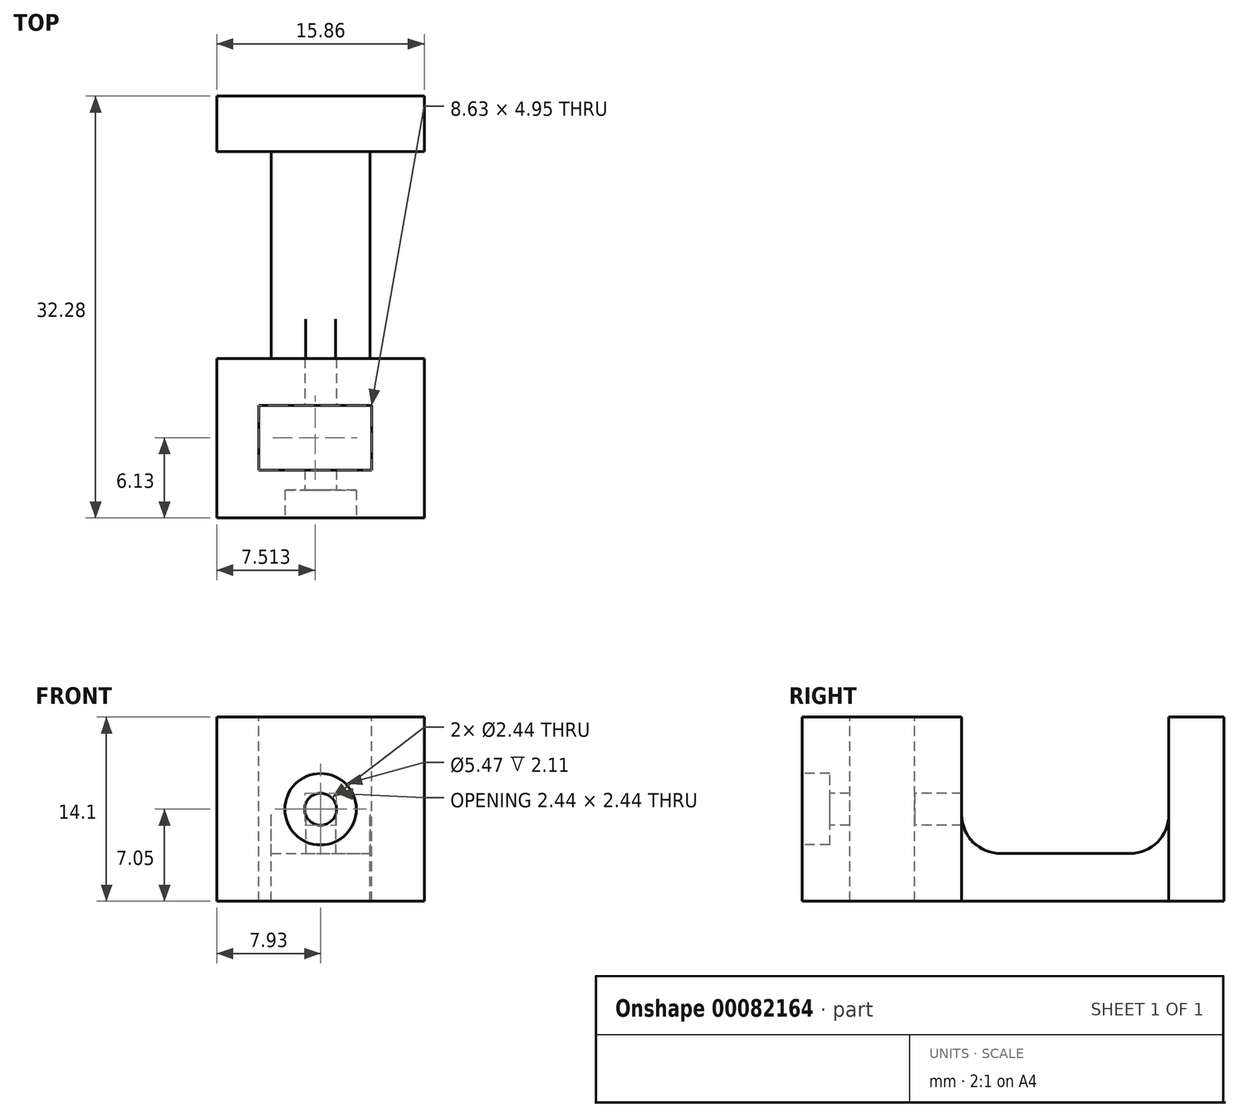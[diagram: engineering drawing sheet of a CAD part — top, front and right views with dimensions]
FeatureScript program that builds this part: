
annotation { "Feature Type Name" : "Feature", "Feature Type Description" : "" }
export const myFeature = defineFeature(function(context is Context, id is Id, definition is map)
    precondition{}
    {
        {
            var Q0;
            Q0=qCreatedBy(makeId("Top.planeOp"),FACE);
            var sketch = newSketch(context, id + "F0", { "sketchPlane" : qUnion([Q0])});
            skLineSegment(sketch, "E0.bottom", {"start": v(7.94, 16.14) * mm, "end": v(-7.93, 16.14) * mm});
            skLineSegment(sketch, "E0.top", {"start": v(7.93, -16.14) * mm, "end": v(-7.94, -16.14) * mm});
            skLineSegment(sketch, "E0.left", {"start": v(7.94, 16.14) * mm, "end": v(7.93, -16.14) * mm});
            skLineSegment(sketch, "E0.right", {"start": v(-7.93, 16.14) * mm, "end": v(-7.94, -16.14) * mm});
            skPoint(sketch, "E0.middle", {"position": v(0, 0) * mm});
            skSolve(sketch);
        }
        {
            var Q0;
            Q0 = qSketchRegion(id + "F0", true);
            extrude(context, id + "F1", {"entities" : qUnion([Q0]), "depth" : 14.1 * mm});
        }
        {
            var Q0;
            Q0=makeQuery(id+"F1.opExtrude","CAP_FACE",FACE,{"disambiguationData":[OSD([sQuery(id+"F0.wireOp",EDGE,"E0.bottom"),sQuery(id+"F0.wireOp",EDGE,"E0.top"),sQuery(id+"F0.wireOp",EDGE,"E0.left"),sQuery(id+"F0.wireOp",EDGE,"E0.right")])],"isStart":false});
            var sketch = newSketch(context, id + "F2", { "sketchPlane" : qUnion([Q0])});
            skLineSegment(sketch, "E1.bottom", {"start": v(-7.93, 11.9) * mm, "end": v(7.94, 11.9) * mm});
            skLineSegment(sketch, "E1.top", {"start": v(-7.93, -3.94) * mm, "end": v(7.94, -3.94) * mm});
            skLineSegment(sketch, "E1.left", {"start": v(-7.93, 11.9) * mm, "end": v(-7.93, -3.94) * mm});
            skLineSegment(sketch, "E1.right", {"start": v(7.94, 11.9) * mm, "end": v(7.94, -3.94) * mm});
            skSolve(sketch);
        }
        {
            var Q0;
            Q0 = qSketchRegion(id + "F2", true);
            extrude(context, id + "F3", {"entities" : qUnion([Q0]), "operationType" : NewBodyOperationType.REMOVE, "oppositeDirection" : true, "depth" : 10.45 * mm});
        }
        {
            var Q0;
            Q0=makeQuery(id+"F3.boolean.opBoolean","COPY",FACE,{"derivedFrom":makeQuery(id+"F3.opExtrude","CAP_FACE",FACE,{"disambiguationData":[OSD([sQuery(id+"F2.wireOp",EDGE,"E1.bottom"),sQuery(id+"F2.wireOp",EDGE,"E1.top"),sQuery(id+"F2.wireOp",EDGE,"E1.left"),sQuery(id+"F2.wireOp",EDGE,"E1.right")])],"isStart":false})});
            var sketch = newSketch(context, id + "F4", { "sketchPlane" : qUnion([Q0])});
            skLineSegment(sketch, "E2.bottom", {"start": v(3.77, 11.9) * mm, "end": v(7.93, 11.9) * mm});
            skLineSegment(sketch, "E2.top", {"start": v(3.77, -3.94) * mm, "end": v(7.93, -3.94) * mm});
            skLineSegment(sketch, "E2.left", {"start": v(3.77, 11.9) * mm, "end": v(3.78, -3.94) * mm});
            skLineSegment(sketch, "E2.right", {"start": v(7.94, 11.9) * mm, "end": v(7.94, -3.94) * mm});
            skLineSegment(sketch, "E3.bottom", {"start": v(-7.93, 11.9) * mm, "end": v(-3.77, 11.9) * mm});
            skLineSegment(sketch, "E3.top", {"start": v(-7.93, -3.94) * mm, "end": v(-3.77, -3.94) * mm});
            skLineSegment(sketch, "E3.left", {"start": v(-7.93, 11.9) * mm, "end": v(-7.93, -3.94) * mm});
            skLineSegment(sketch, "E3.right", {"start": v(-3.77, 11.9) * mm, "end": v(-3.77, -3.94) * mm});
            skSolve(sketch);
        }
        {
            var Q0;
            Q0 = qSketchRegion(id + "F4", true);
            extrude(context, id + "F5", {"entities" : qUnion([Q0]), "operationType" : NewBodyOperationType.REMOVE, "endBound" : BoundingType.UP_TO_NEXT, "oppositeDirection" : true, "depth" : 25 * mm});
        }
        {
            var Q0;
            {var subQ0=sQuery(id+"F0.wireOp",EDGE,"E0.top");var subQ1=sQuery(id+"F0.wireOp",EDGE,"E0.left");var subQ2=sQuery(id+"F0.wireOp",EDGE,"E0.right");Q0=makeQuery(id+"F3.boolean.opBoolean","SPLIT",FACE,{"disambiguationData":[TD([makeQuery(id+"F1.opExtrude","SWEPT_FACE",FACE,{"disambiguationData":[OSD([subQ0])]})])],"derivedFrom":makeQuery(id+"F1.opExtrude","CAP_FACE",FACE,{"disambiguationData":[OSD([sQuery(id+"F0.wireOp",EDGE,"E0.bottom"),subQ0,subQ1,subQ2])],"isStart":false})});}
            var sketch = newSketch(context, id + "F6", { "sketchPlane" : qUnion([Q0])});
            skLineSegment(sketch, "E4.bottom", {"start": v(3.9, -12.49) * mm, "end": v(-4.73, -12.49) * mm});
            skLineSegment(sketch, "E4.top", {"start": v(3.9, -7.54) * mm, "end": v(-4.73, -7.54) * mm});
            skLineSegment(sketch, "E4.left", {"start": v(3.9, -12.49) * mm, "end": v(3.9, -7.54) * mm});
            skLineSegment(sketch, "E4.right", {"start": v(-4.73, -12.49) * mm, "end": v(-4.73, -7.54) * mm});
            skSolve(sketch);
        }
        {
            var Q0;
            Q0 = qSketchRegion(id + "F6", true);
            extrude(context, id + "F7", {"entities" : qUnion([Q0]), "operationType" : NewBodyOperationType.REMOVE, "endBound" : BoundingType.UP_TO_NEXT, "oppositeDirection" : true, "depth" : 25 * mm});
        }
        {
            var Q0;
            Q0=makeQuery(id+"F1.opExtrude","SWEPT_FACE",FACE,{"disambiguationData":[OSD([sQuery(id+"F0.wireOp",EDGE,"E0.top")])]});
            var sketch = newSketch(context, id + "F8", { "sketchPlane" : qUnion([Q0])});
            skCircle(sketch, "E5", {"center": v(0, 7.05) * mm, "radius": 1.22 * mm});
            skSolve(sketch);
        }
        {
            var Q0;
            Q0 = qSketchRegion(id + "F8", true);
            extrude(context, id + "F9", {"entities" : qUnion([Q0]), "operationType" : NewBodyOperationType.REMOVE, "oppositeDirection" : true, "depth" : 12.5 * mm});
        }
        {
            var Q0;
            Q0=makeQuery(id+"F1.opExtrude","SWEPT_FACE",FACE,{"disambiguationData":[OSD([sQuery(id+"F0.wireOp",EDGE,"E0.top")])]});
            var sketch = newSketch(context, id + "F10", { "sketchPlane" : qUnion([Q0])});
            skCircle(sketch, "E6", {"center": v(0, 7.05) * mm, "radius": 2.73 * mm});
            skSolve(sketch);
        }
        {
            var Q0;
            Q0 = qSketchRegion(id + "F10", true);
            extrude(context, id + "F11", {"entities" : qUnion([Q0]), "operationType" : NewBodyOperationType.REMOVE, "oppositeDirection" : true, "depth" : 2.1 * mm});
        }
        {
            var Q0;
            Q0=makeQuery(id+"F3.boolean.opBoolean","COPY",EDGE,{"derivedFrom":makeQuery(id+"F3.opExtrude","CAP_EDGE",EDGE,{"disambiguationData":[OSD([sQuery(id+"F2.wireOp",EDGE,"E1.top")])],"isStart":false})});
            fillet(context, id + "F12", {"entities" : qUnion([Q0]), "radius" : 3 * mm, "tangentPropagation" : true, "allowEdgeOverflow" : false});
        }
        {
            var Q0;
            Q0=makeQuery(id+"F3.boolean.opBoolean","COPY",EDGE,{"derivedFrom":makeQuery(id+"F3.opExtrude","CAP_EDGE",EDGE,{"disambiguationData":[OSD([sQuery(id+"F2.wireOp",EDGE,"E1.bottom")])],"isStart":false})});
            fillet(context, id + "F13", {"entities" : qUnion([Q0]), "radius" : 3 * mm, "tangentPropagation" : true, "allowEdgeOverflow" : false});
        }
    });
